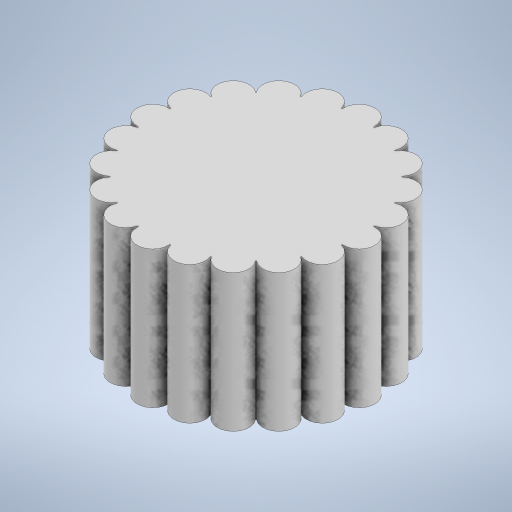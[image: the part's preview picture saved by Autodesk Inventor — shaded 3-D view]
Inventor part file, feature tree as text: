
AUTODESK INVENTOR PART (.ipt)
format: ipt  version: 2023 (Build 270158000, 158)  size: 398,336 bytes
history: native  units: mm
features: extrude x3, sketch x3, other x1, projected_geometry x1
ambient origin geometry x8: Origin, YZ Plane, XZ Plane, XY Plane, X Axis, Y Axis, Z Axis, Center Point
bodies: Body1 (feature_tree)
feature tree (8):
  other  "솔리드1"
  extrude  "돌출1"  Depth=7.8mm
  extrude  "돌출2"  Depth=5.0mm TaperAngle=0.0deg
  extrude  "돌출3"  Depth=16.5mm
  sketch  "스케치1"
  sketch  "스케치2"
  sketch  "스케치3"
  projected_geometry  "투영된 루프1"
